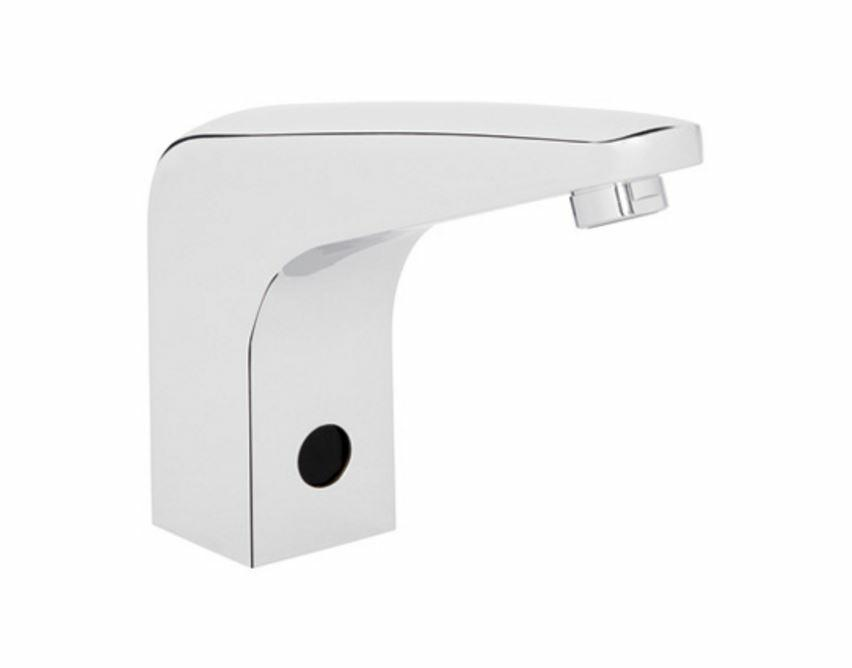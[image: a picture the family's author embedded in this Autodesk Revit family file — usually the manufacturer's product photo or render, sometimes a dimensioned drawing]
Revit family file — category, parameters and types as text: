
# Revit family: Llave Electronica TV-304
name_source: partatom
category: Aparatos sanitarios
revit_build: Autodesk Revit 2016 (Build: 20150220_1215(x64)
units: mm (PartAtom-declared; Revit-internal decimal feet)

## family parameters
Compartido = Sí
Corte con vacíos al cargar = No
Cota de conector redondo = Diámetro de uso
Número OmniClass = 23.45.55.14
Punto de cálculo de habitación = Sí
Se basa en plano de trabajo = No
Siempre vertical = Sí
Tipo de pieza = Normal
Título OmniClass = Single Faucets

## types (1)
- TV-304
    Batteries = 4 Baterías AA
    Certification = http://www.helvex.com.mx
    Chrome = Brass Chromed
    Comentarios de tipo = Electronic Line
    Conexión AF = Sí
    Connection = ½" - 14 NPSM
    Descripción = Llave electrónica de sensor de baterías
    Detection Range = 1.9" (50 mm) - 8.7" (220 mm)
    Documentation = http://www.helvex.com.mx
    Fabricante = Helvex
    Features = Infrared Sensor, Filter with Check Valve Maintenance
    Feeding Voltage = 6 V
    Imagen de tipo = TV-304.JPG
    Instructive = http://www.helvex.com.mx
    Max. Working Pressure = 85.3 psi
    Min. Working Pressure = 5.7 psi
    Modelo = TV-304
    URL = http://www.helvex.com.mx

## geometry (parser evidence)
native form markers: Sweep x3
no freeform markers — native parametric forms only
